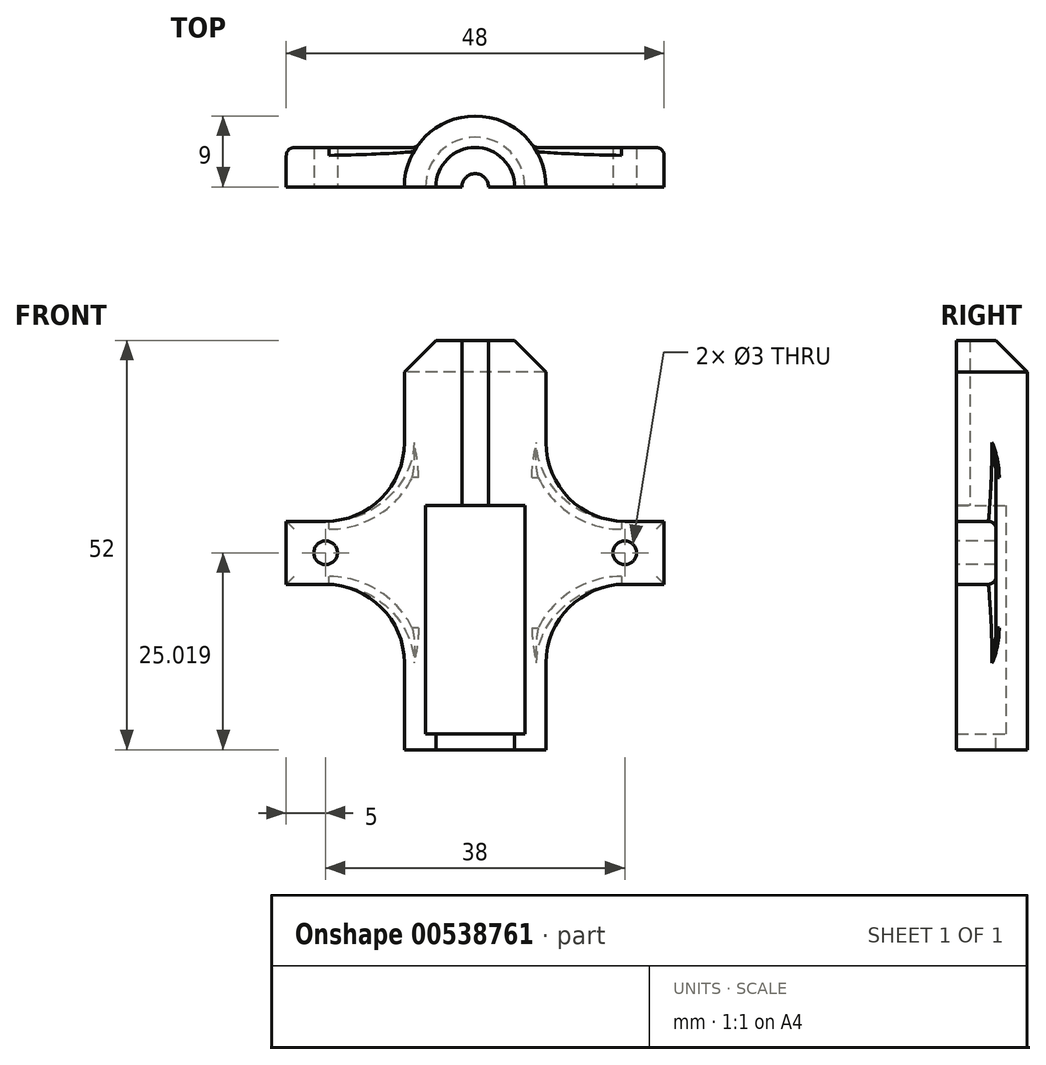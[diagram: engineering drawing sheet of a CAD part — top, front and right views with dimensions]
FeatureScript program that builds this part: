
annotation { "Feature Type Name" : "Feature", "Feature Type Description" : "" }
export const myFeature = defineFeature(function(context is Context, id is Id, definition is map)
    precondition{}
    {
        {
            var Q0;
            Q0=qCreatedBy(makeId("Top.planeOp"),FACE);
            var sketch = newSketch(context, id + "F0", { "sketchPlane" : qUnion([Q0])});
            skArc(sketch, "E0", {"start": v(9, 0) * mm, "mid": v(0, 9) * mm, "end": v(-9, 0) * mm});
            skArc(sketch, "E1", {"start": v(1.69, 0) * mm, "mid": v(0, 1.69) * mm, "end": v(-1.69, 0) * mm});
            skLineSegment(sketch, "E2", {"start": v(-9, 0) * mm, "end": v(-1.69, 0) * mm});
            skLineSegment(sketch, "E3.trimOffspring", {"start": v(1.69, 0) * mm, "end": v(9, 0) * mm});
            skSolve(sketch);
        }
        {
            var Q0;
            Q0 = qSketchRegion(id + "F0", true);
            extrude(context, id + "F1", {"entities" : qUnion([Q0]), "depth" : 21 * mm, "offsetDistance" : 25 * mm});
        }
        {
            var Q0;
            Q0=makeQuery(id+"F1.opExtrude","CAP_FACE",FACE,{"disambiguationData":[OSD([sQuery(id+"F0.wireOp",EDGE,"E0"),sQuery(id+"F0.wireOp",EDGE,"E1"),sQuery(id+"F0.wireOp",EDGE,"E2"),sQuery(id+"F0.wireOp",EDGE,"E3.trimOffspring")])],"isStart":true});
            var sketch = newSketch(context, id + "F2", { "sketchPlane" : qUnion([Q0])});
            skArc(sketch, "E4", {"start": v(-9, 0) * mm, "mid": v(0, -9) * mm, "end": v(9, 0) * mm});
            skLineSegment(sketch, "E5", {"start": v(-9, 0) * mm, "end": v(-6.3, 0) * mm});
            skArc(sketch, "E6", {"start": v(-6.3, 0) * mm, "mid": v(0, -6.3) * mm, "end": v(6.3, 0) * mm});
            skLineSegment(sketch, "E7.trimOffspring", {"start": v(6.3, 0) * mm, "end": v(9, 0) * mm});
            skSolve(sketch);
        }
        {
            var Q0;
            Q0 = qSketchRegion(id + "F2", true);
            extrude(context, id + "F3", {"entities" : qUnion([Q0]), "operationType" : NewBodyOperationType.ADD, "depth" : 29 * mm, "offsetDistance" : 25 * mm});
        }
        {
            var Q0;
            Q0=makeQuery(id+"F3.opExtrude","CAP_FACE",FACE,{"disambiguationData":[OSD([sQuery(id+"F2.wireOp",EDGE,"E4"),sQuery(id+"F2.wireOp",EDGE,"E5"),sQuery(id+"F2.wireOp",EDGE,"E6"),sQuery(id+"F2.wireOp",EDGE,"E7.trimOffspring")])],"isStart":false});
            var sketch = newSketch(context, id + "F4", { "sketchPlane" : qUnion([Q0])});
            skArc(sketch, "E8", {"start": v(-9, 0) * mm, "mid": v(0, -9) * mm, "end": v(9, 0) * mm});
            skLineSegment(sketch, "E9", {"start": v(-9, 0) * mm, "end": v(-5, 0) * mm});
            skArc(sketch, "E10", {"start": v(-5, 0) * mm, "mid": v(0, -5) * mm, "end": v(5, 0) * mm});
            skLineSegment(sketch, "E11.trimOffspring", {"start": v(5, 0) * mm, "end": v(9, 0) * mm});
            skSolve(sketch);
        }
        {
            var Q0;
            Q0 = qSketchRegion(id + "F4", true);
            extrude(context, id + "F5", {"entities" : qUnion([Q0]), "operationType" : NewBodyOperationType.ADD, "depth" : 2 * mm, "offsetDistance" : 25 * mm});
        }
        {
            var Q0;
            Q0=makeQuery(id+"F5.boolean.opBoolean","MERGE",FACE,{"derivedFrom":[makeQuery(id+"F3.boolean.opBoolean","MERGE",FACE,{"derivedFrom":[makeQuery(id+"F1.opExtrude","SWEPT_FACE",FACE,{"disambiguationData":[OSD([sQuery(id+"F0.wireOp",EDGE,"E3.trimOffspring")])]}),makeQuery(id+"F3.opExtrude","SWEPT_FACE",FACE,{"disambiguationData":[OSD([sQuery(id+"F2.wireOp",EDGE,"E7.trimOffspring")])]})]}),makeQuery(id+"F5.opExtrude","SWEPT_FACE",FACE,{"disambiguationData":[OSD([sQuery(id+"F4.wireOp",EDGE,"E11.trimOffspring")])]})]});
            var sketch = newSketch(context, id + "F6", { "sketchPlane" : qUnion([Q0])});
            skLineSegment(sketch, "E12.bottom", {"start": v(6.3, -1.98) * mm, "end": v(24, -1.98) * mm});
            skLineSegment(sketch, "E12.top", {"start": v(6.3, -9.98) * mm, "end": v(24, -9.98) * mm});
            skLineSegment(sketch, "E12.left", {"start": v(6.3, -1.98) * mm, "end": v(6.3, -9.98) * mm});
            skLineSegment(sketch, "E12.right", {"start": v(24, -1.98) * mm, "end": v(24, -9.98) * mm});
            skCircle(sketch, "E13", {"center": v(19, -5.98) * mm, "radius": 1.5 * mm});
            skLineSegment(sketch, "E14", {"start": v(0, 21) * mm, "end": v(0, -31) * mm, "construction": true});
            skLineSegment(sketch, "E15.MirrorCS", {"start": v(-6.3, -1.98) * mm, "end": v(-24, -1.98) * mm});
            skLineSegment(sketch, "E16.MirrorCS", {"start": v(-6.3, -9.98) * mm, "end": v(-24, -9.98) * mm});
            skLineSegment(sketch, "E17.MirrorCS", {"start": v(-6.3, -1.98) * mm, "end": v(-6.3, -9.98) * mm});
            skCircle(sketch, "E18.MirrorC", {"center": v(-19, -5.98) * mm, "radius": 1.5 * mm});
            skLineSegment(sketch, "E19.MirrorCS", {"start": v(-24, -1.98) * mm, "end": v(-24, -9.98) * mm});
            skSolve(sketch);
        }
        {
            var Q0;
            Q0 = qSketchRegion(id + "F6", true);
            extrude(context, id + "F7", {"entities" : qUnion([Q0]), "operationType" : NewBodyOperationType.ADD, "oppositeDirection" : true, "depth" : 5 * mm, "offsetDistance" : 25 * mm});
        }
        {
            var Q0;
            Q0=makeQuery(id+"F7.boolean.opBoolean","INTERSECT",EDGE,{"derivedFrom":[makeQuery(id+"F5.boolean.opBoolean","MERGE",FACE,{"derivedFrom":[makeQuery(id+"F3.boolean.opBoolean","MERGE",FACE,{"derivedFrom":[makeQuery(id+"F1.opExtrude","SWEPT_FACE",FACE,{"disambiguationData":[OSD([sQuery(id+"F0.wireOp",EDGE,"E0")])]}),makeQuery(id+"F3.opExtrude","SWEPT_FACE",FACE,{"disambiguationData":[OSD([sQuery(id+"F2.wireOp",EDGE,"E4")])]})]}),makeQuery(id+"F5.opExtrude","SWEPT_FACE",FACE,{"disambiguationData":[OSD([sQuery(id+"F4.wireOp",EDGE,"E8")])]})]}),makeQuery(id+"F7.opExtrude","SWEPT_FACE",FACE,{"disambiguationData":[OSD([sQuery(id+"F6.wireOp",EDGE,"E12.bottom")])]})]});
            var Q1;
            Q1=makeQuery(id+"F7.boolean.opBoolean","INTERSECT",EDGE,{"derivedFrom":[makeQuery(id+"F5.boolean.opBoolean","MERGE",FACE,{"derivedFrom":[makeQuery(id+"F3.boolean.opBoolean","MERGE",FACE,{"derivedFrom":[makeQuery(id+"F1.opExtrude","SWEPT_FACE",FACE,{"disambiguationData":[OSD([sQuery(id+"F0.wireOp",EDGE,"E0")])]}),makeQuery(id+"F3.opExtrude","SWEPT_FACE",FACE,{"disambiguationData":[OSD([sQuery(id+"F2.wireOp",EDGE,"E4")])]})]}),makeQuery(id+"F5.opExtrude","SWEPT_FACE",FACE,{"disambiguationData":[OSD([sQuery(id+"F4.wireOp",EDGE,"E8")])]})]}),makeQuery(id+"F7.opExtrude","SWEPT_FACE",FACE,{"disambiguationData":[OSD([sQuery(id+"F6.wireOp",EDGE,"E12.top")])]})]});
            var Q2;
            Q2=makeQuery(id+"F7.boolean.opBoolean","INTERSECT",EDGE,{"derivedFrom":[makeQuery(id+"F5.boolean.opBoolean","MERGE",FACE,{"derivedFrom":[makeQuery(id+"F3.boolean.opBoolean","MERGE",FACE,{"derivedFrom":[makeQuery(id+"F1.opExtrude","SWEPT_FACE",FACE,{"disambiguationData":[OSD([sQuery(id+"F0.wireOp",EDGE,"E0")])]}),makeQuery(id+"F3.opExtrude","SWEPT_FACE",FACE,{"disambiguationData":[OSD([sQuery(id+"F2.wireOp",EDGE,"E4")])]})]}),makeQuery(id+"F5.opExtrude","SWEPT_FACE",FACE,{"disambiguationData":[OSD([sQuery(id+"F4.wireOp",EDGE,"E8")])]})]}),makeQuery(id+"F7.opExtrude","SWEPT_FACE",FACE,{"disambiguationData":[OSD([sQuery(id+"F6.wireOp",EDGE,"E16.MirrorCS")])]})]});
            var Q3;
            Q3=makeQuery(id+"F7.boolean.opBoolean","INTERSECT",EDGE,{"derivedFrom":[makeQuery(id+"F5.boolean.opBoolean","MERGE",FACE,{"derivedFrom":[makeQuery(id+"F3.boolean.opBoolean","MERGE",FACE,{"derivedFrom":[makeQuery(id+"F1.opExtrude","SWEPT_FACE",FACE,{"disambiguationData":[OSD([sQuery(id+"F0.wireOp",EDGE,"E0")])]}),makeQuery(id+"F3.opExtrude","SWEPT_FACE",FACE,{"disambiguationData":[OSD([sQuery(id+"F2.wireOp",EDGE,"E4")])]})]}),makeQuery(id+"F5.opExtrude","SWEPT_FACE",FACE,{"disambiguationData":[OSD([sQuery(id+"F4.wireOp",EDGE,"E8")])]})]}),makeQuery(id+"F7.opExtrude","SWEPT_FACE",FACE,{"disambiguationData":[OSD([sQuery(id+"F6.wireOp",EDGE,"E15.MirrorCS")])]})]});
            fillet(context, id + "F8", {"entities" : qUnion([Q0, Q1, Q2, Q3]), "radius" : 10 * mm, "tangentPropagation" : true, "allowEdgeOverflow" : false});
        }
        {
            var Q0;
            Q0=makeQuery(id+"F7.opExtrude","CAP_EDGE",EDGE,{"disambiguationData":[OSD([sQuery(id+"F6.wireOp",EDGE,"E19.MirrorCS")])],"isStart":false});
            var Q1;
            Q1=makeQuery(id+"F7.opExtrude","CAP_EDGE",EDGE,{"disambiguationData":[OSD([sQuery(id+"F6.wireOp",EDGE,"E15.MirrorCS")])],"isStart":false});
            var Q2;
            Q2=makeQuery(id+"F7.opExtrude","CAP_EDGE",EDGE,{"disambiguationData":[OSD([sQuery(id+"F6.wireOp",EDGE,"E16.MirrorCS")])],"isStart":false});
            var Q3;
            Q3=makeQuery(id+"F7.opExtrude","CAP_EDGE",EDGE,{"disambiguationData":[OSD([sQuery(id+"F6.wireOp",EDGE,"E12.right")])],"isStart":false});
            var Q4;
            Q4=makeQuery(id+"F7.opExtrude","CAP_EDGE",EDGE,{"disambiguationData":[OSD([sQuery(id+"F6.wireOp",EDGE,"E12.top")])],"isStart":false});
            var Q5;
            Q5=makeQuery(id+"F7.opExtrude","CAP_EDGE",EDGE,{"disambiguationData":[OSD([sQuery(id+"F6.wireOp",EDGE,"E12.bottom")])],"isStart":false});
            var Q6;
            Q6=makeQuery(id+"F7.boolean.opBoolean","INTERSECT",EDGE,{"derivedFrom":[makeQuery(id+"F5.boolean.opBoolean","MERGE",FACE,{"derivedFrom":[makeQuery(id+"F3.boolean.opBoolean","MERGE",FACE,{"derivedFrom":[makeQuery(id+"F1.opExtrude","SWEPT_FACE",FACE,{"disambiguationData":[OSD([sQuery(id+"F0.wireOp",EDGE,"E0")])]}),makeQuery(id+"F3.opExtrude","SWEPT_FACE",FACE,{"disambiguationData":[OSD([sQuery(id+"F2.wireOp",EDGE,"E4")])]})]}),makeQuery(id+"F5.opExtrude","SWEPT_FACE",FACE,{"disambiguationData":[OSD([sQuery(id+"F4.wireOp",EDGE,"E8")])]})]}),makeQuery(id+"F7.opExtrude","CAP_FACE",FACE,{"disambiguationData":[OSD([sQuery(id+"F6.wireOp",EDGE,"E12.bottom"),sQuery(id+"F6.wireOp",EDGE,"E12.top"),sQuery(id+"F6.wireOp",EDGE,"E12.left"),sQuery(id+"F6.wireOp",EDGE,"E12.right"),sQuery(id+"F6.wireOp",EDGE,"E13")])],"isStart":false})]});
            var Q7;
            Q7=makeQuery(id+"F7.boolean.opBoolean","INTERSECT",EDGE,{"derivedFrom":[makeQuery(id+"F5.boolean.opBoolean","MERGE",FACE,{"derivedFrom":[makeQuery(id+"F3.boolean.opBoolean","MERGE",FACE,{"derivedFrom":[makeQuery(id+"F1.opExtrude","SWEPT_FACE",FACE,{"disambiguationData":[OSD([sQuery(id+"F0.wireOp",EDGE,"E0")])]}),makeQuery(id+"F3.opExtrude","SWEPT_FACE",FACE,{"disambiguationData":[OSD([sQuery(id+"F2.wireOp",EDGE,"E4")])]})]}),makeQuery(id+"F5.opExtrude","SWEPT_FACE",FACE,{"disambiguationData":[OSD([sQuery(id+"F4.wireOp",EDGE,"E8")])]})]}),makeQuery(id+"F7.opExtrude","CAP_FACE",FACE,{"disambiguationData":[OSD([sQuery(id+"F6.wireOp",EDGE,"E15.MirrorCS"),sQuery(id+"F6.wireOp",EDGE,"E16.MirrorCS"),sQuery(id+"F6.wireOp",EDGE,"E17.MirrorCS"),sQuery(id+"F6.wireOp",EDGE,"E18.MirrorC"),sQuery(id+"F6.wireOp",EDGE,"E19.MirrorCS")])],"isStart":false})]});
            fillet(context, id + "F9", {"entities" : qUnion([Q0, Q1, Q2, Q3, Q4, Q5, Q6, Q7]), "radius" : 1 * mm, "tangentPropagation" : true, "allowEdgeOverflow" : false});
        }
        {
            var Q0;
            Q0=makeQuery(id+"F1.opExtrude","CAP_EDGE",EDGE,{"disambiguationData":[OSD([sQuery(id+"F0.wireOp",EDGE,"E0")])],"isStart":false});
            chamfer(context, id + "F10", {"entities" : qUnion([Q0]), "width" : 4 * mm, "tangentPropagation" : true});
        }
    });
